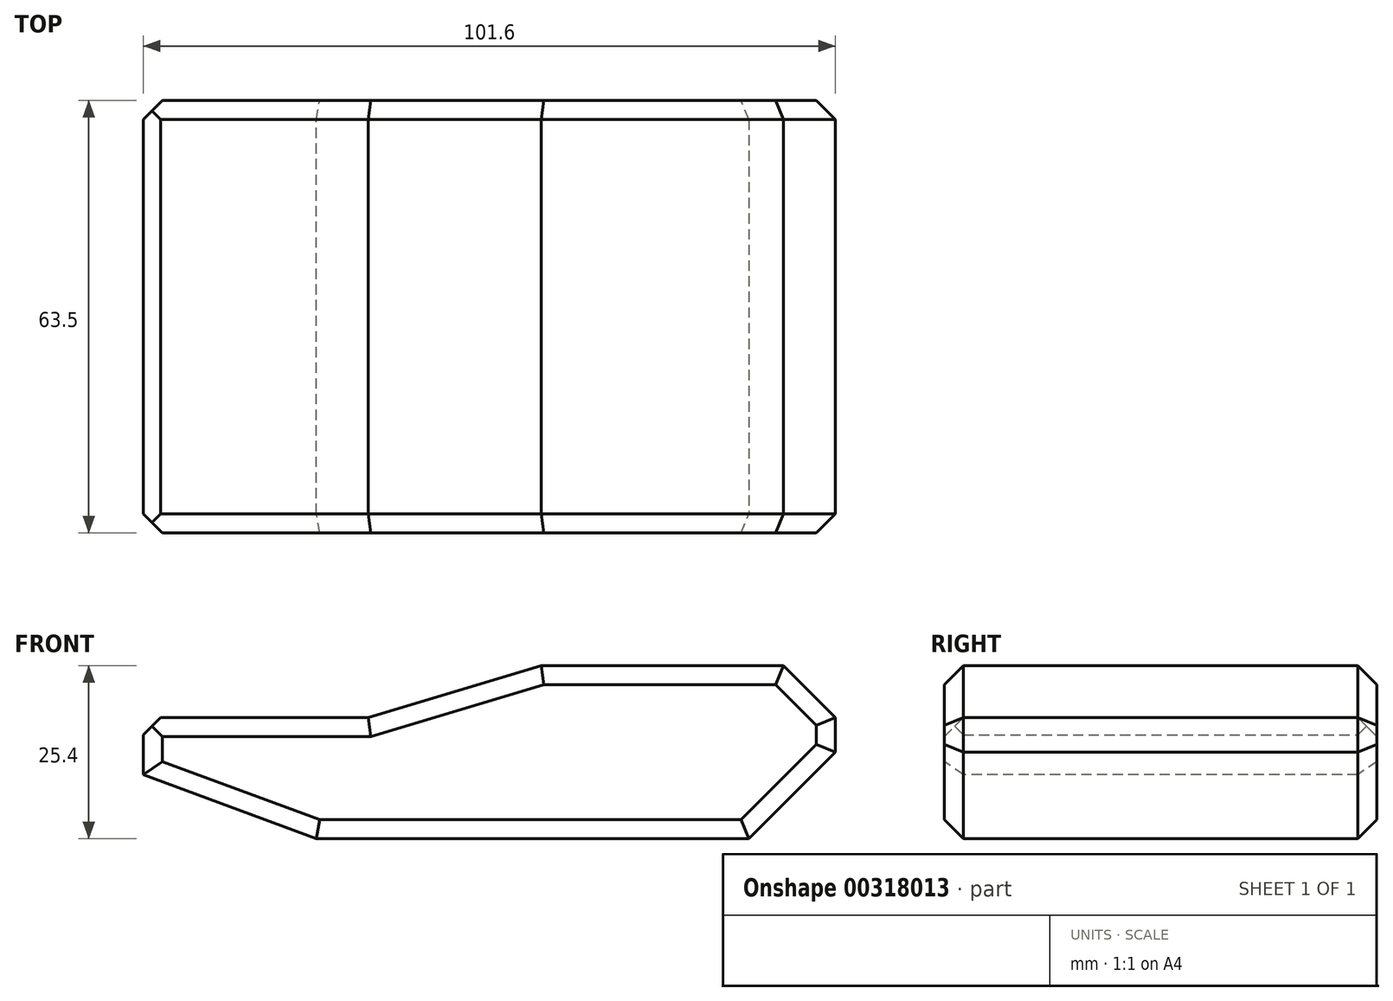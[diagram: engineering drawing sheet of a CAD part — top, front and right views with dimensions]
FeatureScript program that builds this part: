
annotation { "Feature Type Name" : "Feature", "Feature Type Description" : "" }
export const myFeature = defineFeature(function(context is Context, id is Id, definition is map)
    precondition{}
    {
        {
            var Q0;
            Q0=qCreatedBy(makeId("Front.planeOp"),FACE);
            var sketch = newSketch(context, id + "F0", { "sketchPlane" : qUnion([Q0])});
            skLineSegment(sketch, "E0.bottom", {"start": v(-65.25, 21.28) * mm, "end": v(36.35, 21.28) * mm});
            skLineSegment(sketch, "E0.top", {"start": v(-65.25, 3.5) * mm, "end": v(36.35, 3.5) * mm});
            skLineSegment(sketch, "E0.left", {"start": v(-65.25, 21.28) * mm, "end": v(-65.25, 3.5) * mm});
            skLineSegment(sketch, "E0.right", {"start": v(36.35, 21.28) * mm, "end": v(36.35, 3.5) * mm});
            skSolve(sketch);
        }
        {
            var Q0;
            Q0=makeQuery(id+"F0.imprint","IMPRINT",FACE,{"disambiguationData":[TD([[makeQuery(id+"F0.imprint","IMPRINT",EDGE,{"derivedFrom":sQuery(id+"F0.wireOp",EDGE,"E0.bottom")}),-1.0]])]});
            extrude(context, id + "F1", {"entities" : qUnion([Q0]), "depth" : 63.5 * mm});
        }
        {
            var Q0;
            Q0=makeQuery(id+"F1.opExtrude","SWEPT_EDGE",EDGE,{"disambiguationData":[OSD([sQuery(id+"F0.wireOp",EDGE,"E0.top"),sQuery(id+"F0.wireOp",EDGE,"E0.left")])]});
            chamfer(context, id + "F2", {"entities" : qUnion([Q0]), "chamferType" : ChamferType.TWO_OFFSETS, "width1" : 25.4 * mm, "oppositeDirection" : false, "width2" : 9.4 * mm, "tangentPropagation" : true});
        }
        {
            var Q0;
            Q0=makeQuery(id+"F1.opExtrude","SWEPT_EDGE",EDGE,{"disambiguationData":[OSD([sQuery(id+"F0.wireOp",EDGE,"E0.top"),sQuery(id+"F0.wireOp",EDGE,"E0.right")])]});
            chamfer(context, id + "F3", {"entities" : qUnion([Q0]), "width" : 12.7 * mm, "tangentPropagation" : true});
        }
        {
            var Q0;
            Q0=makeQuery(id+"F1.opExtrude","CAP_FACE",FACE,{"disambiguationData":[OSD([sQuery(id+"F0.wireOp",EDGE,"E0.bottom"),sQuery(id+"F0.wireOp",EDGE,"E0.top"),sQuery(id+"F0.wireOp",EDGE,"E0.left"),sQuery(id+"F0.wireOp",EDGE,"E0.right")])],"isStart":true});
            var sketch = newSketch(context, id + "F4", { "sketchPlane" : qUnion([Q0])});
            skLineSegment(sketch, "E1.bottom", {"start": v(-36.35, 21.28) * mm, "end": v(32.23, 21.28) * mm});
            skLineSegment(sketch, "E1.top", {"start": v(-36.35, 28.9) * mm, "end": v(32.23, 28.9) * mm});
            skLineSegment(sketch, "E1.left", {"start": v(-36.35, 21.28) * mm, "end": v(-36.35, 28.9) * mm});
            skLineSegment(sketch, "E1.right", {"start": v(32.23, 21.28) * mm, "end": v(32.23, 28.9) * mm});
            skSolve(sketch);
        }
        {
            var Q0;
            Q0=makeQuery(id+"F4.imprint","IMPRINT",FACE,{"disambiguationData":[TD([[makeQuery(id+"F4.imprint","IMPRINT",EDGE,{"derivedFrom":sQuery(id+"F4.wireOp",EDGE,"E1.bottom")}),-1.0]])]});
            extrude(context, id + "F5", {"entities" : qUnion([Q0]), "operationType" : NewBodyOperationType.ADD, "oppositeDirection" : true, "depth" : 63.5 * mm});
        }
        {
            var Q0;
            Q0=makeQuery(id+"F5.opExtrude","SWEPT_EDGE",EDGE,{"disambiguationData":[OSD([sQuery(id+"F4.wireOp",EDGE,"E1.top"),sQuery(id+"F4.wireOp",EDGE,"E1.left")])]});
            chamfer(context, id + "F6", {"entities" : qUnion([Q0]), "chamferType" : ChamferType.TWO_OFFSETS, "width1" : 7.62 * mm, "oppositeDirection" : false, "width2" : 7.62 * mm, "tangentPropagation" : true});
        }
        {
            var Q0;
            Q0=makeQuery(id+"F5.opExtrude","SWEPT_EDGE",EDGE,{"disambiguationData":[OSD([sQuery(id+"F4.wireOp",EDGE,"E1.top"),sQuery(id+"F4.wireOp",EDGE,"E1.right")])]});
            chamfer(context, id + "F7", {"entities" : qUnion([Q0]), "chamferType" : ChamferType.TWO_OFFSETS, "width1" : 7.62 * mm, "oppositeDirection" : false, "width2" : 25.4 * mm, "tangentPropagation" : true});
        }
        {
            var Q0;
            Q0=makeQuery(id+"F1.opExtrude","CAP_EDGE",EDGE,{"disambiguationData":[OSD([sQuery(id+"F0.wireOp",EDGE,"E0.left")])],"isStart":true});
            var Q1;
            Q1=makeQuery(id+"F1.opExtrude","CAP_EDGE",EDGE,{"disambiguationData":[OSD([sQuery(id+"F0.wireOp",EDGE,"E0.left")])],"isStart":false});
            var Q2;
            {var subQ0=sQuery(id+"F0.wireOp",EDGE,"E0.left");var subQ1=sQuery(id+"F0.wireOp",EDGE,"E0.top");Q2=makeQuery(id+"F2.opChamfer","BLEND_EDGE",EDGE,{"blendedFrom":[makeQuery(id+"F1.opExtrude","SWEPT_EDGE",EDGE,{"disambiguationData":[OSD([subQ1,subQ0])]}),makeQuery(id+"F1.opExtrude","CAP_FACE",FACE,{"disambiguationData":[OSD([sQuery(id+"F0.wireOp",EDGE,"E0.bottom"),subQ1,subQ0,sQuery(id+"F0.wireOp",EDGE,"E0.right")])],"isStart":false})],"blendedInto":[makeQuery(id+"F1.opExtrude","CAP_FACE",FACE,{"disambiguationData":[OSD([sQuery(id+"F0.wireOp",EDGE,"E0.bottom"),subQ1,subQ0,sQuery(id+"F0.wireOp",EDGE,"E0.right")])],"isStart":false})]});}
            var Q3;
            {var subQ0=sQuery(id+"F0.wireOp",EDGE,"E0.left");var subQ1=sQuery(id+"F0.wireOp",EDGE,"E0.top");Q3=makeQuery(id+"F2.opChamfer","BLEND_EDGE",EDGE,{"blendedFrom":[makeQuery(id+"F1.opExtrude","SWEPT_EDGE",EDGE,{"disambiguationData":[OSD([subQ1,subQ0])]}),makeQuery(id+"F1.opExtrude","CAP_FACE",FACE,{"disambiguationData":[OSD([sQuery(id+"F0.wireOp",EDGE,"E0.bottom"),subQ1,subQ0,sQuery(id+"F0.wireOp",EDGE,"E0.right")])],"isStart":true})],"blendedInto":[makeQuery(id+"F1.opExtrude","CAP_FACE",FACE,{"disambiguationData":[OSD([sQuery(id+"F0.wireOp",EDGE,"E0.bottom"),subQ1,subQ0,sQuery(id+"F0.wireOp",EDGE,"E0.right")])],"isStart":true})]});}
            var Q4;
            Q4=makeQuery(id+"F1.opExtrude","CAP_EDGE",EDGE,{"disambiguationData":[OSD([sQuery(id+"F0.wireOp",EDGE,"E0.top")])],"isStart":true});
            var Q5;
            Q5=makeQuery(id+"F1.opExtrude","CAP_EDGE",EDGE,{"disambiguationData":[OSD([sQuery(id+"F0.wireOp",EDGE,"E0.top")])],"isStart":false});
            var Q6;
            {var subQ0=sQuery(id+"F4.wireOp",EDGE,"E1.left");var subQ1=sQuery(id+"F4.wireOp",EDGE,"E1.top");Q6=makeQuery(id+"F6.opChamfer","BLEND_EDGE",EDGE,{"blendedFrom":[makeQuery(id+"F5.opExtrude","SWEPT_EDGE",EDGE,{"disambiguationData":[OSD([subQ1,subQ0])]}),makeQuery(id+"F5.boolean.opBoolean","MERGE",FACE,{"derivedFrom":[makeQuery(id+"F1.opExtrude","CAP_FACE",FACE,{"disambiguationData":[OSD([sQuery(id+"F0.wireOp",EDGE,"E0.bottom"),sQuery(id+"F0.wireOp",EDGE,"E0.top"),sQuery(id+"F0.wireOp",EDGE,"E0.left"),sQuery(id+"F0.wireOp",EDGE,"E0.right")])],"isStart":false}),makeQuery(id+"F5.opExtrude","CAP_FACE",FACE,{"disambiguationData":[OSD([sQuery(id+"F4.wireOp",EDGE,"E1.bottom"),subQ1,subQ0,sQuery(id+"F4.wireOp",EDGE,"E1.right")])],"isStart":false})]})],"blendedInto":[makeQuery(id+"F5.boolean.opBoolean","MERGE",FACE,{"derivedFrom":[makeQuery(id+"F1.opExtrude","CAP_FACE",FACE,{"disambiguationData":[OSD([sQuery(id+"F0.wireOp",EDGE,"E0.bottom"),sQuery(id+"F0.wireOp",EDGE,"E0.top"),sQuery(id+"F0.wireOp",EDGE,"E0.left"),sQuery(id+"F0.wireOp",EDGE,"E0.right")])],"isStart":false}),makeQuery(id+"F5.opExtrude","CAP_FACE",FACE,{"disambiguationData":[OSD([sQuery(id+"F4.wireOp",EDGE,"E1.bottom"),subQ1,subQ0,sQuery(id+"F4.wireOp",EDGE,"E1.right")])],"isStart":false})]})]});}
            var Q7;
            Q7=makeQuery(id+"F5.boolean.opBoolean","MERGE",EDGE,{"derivedFrom":[makeQuery(id+"F1.opExtrude","CAP_EDGE",EDGE,{"disambiguationData":[OSD([sQuery(id+"F0.wireOp",EDGE,"E0.right")])],"isStart":false}),makeQuery(id+"F5.opExtrude","CAP_EDGE",EDGE,{"disambiguationData":[OSD([sQuery(id+"F4.wireOp",EDGE,"E1.left")])],"isStart":false})]});
            var Q8;
            {var subQ0=sQuery(id+"F0.wireOp",EDGE,"E0.right");var subQ1=sQuery(id+"F0.wireOp",EDGE,"E0.top");Q8=makeQuery(id+"F3.opChamfer","BLEND_EDGE",EDGE,{"blendedFrom":[makeQuery(id+"F1.opExtrude","SWEPT_EDGE",EDGE,{"disambiguationData":[OSD([subQ1,subQ0])]}),makeQuery(id+"F1.opExtrude","CAP_FACE",FACE,{"disambiguationData":[OSD([sQuery(id+"F0.wireOp",EDGE,"E0.bottom"),subQ1,sQuery(id+"F0.wireOp",EDGE,"E0.left"),subQ0])],"isStart":false})],"blendedInto":[makeQuery(id+"F1.opExtrude","CAP_FACE",FACE,{"disambiguationData":[OSD([sQuery(id+"F0.wireOp",EDGE,"E0.bottom"),subQ1,sQuery(id+"F0.wireOp",EDGE,"E0.left"),subQ0])],"isStart":false})]});}
            var Q9;
            {var subQ0=sQuery(id+"F0.wireOp",EDGE,"E0.right");var subQ1=sQuery(id+"F0.wireOp",EDGE,"E0.top");Q9=makeQuery(id+"F3.opChamfer","BLEND_EDGE",EDGE,{"blendedFrom":[makeQuery(id+"F1.opExtrude","SWEPT_EDGE",EDGE,{"disambiguationData":[OSD([subQ1,subQ0])]}),makeQuery(id+"F1.opExtrude","CAP_FACE",FACE,{"disambiguationData":[OSD([sQuery(id+"F0.wireOp",EDGE,"E0.bottom"),subQ1,sQuery(id+"F0.wireOp",EDGE,"E0.left"),subQ0])],"isStart":true})],"blendedInto":[makeQuery(id+"F1.opExtrude","CAP_FACE",FACE,{"disambiguationData":[OSD([sQuery(id+"F0.wireOp",EDGE,"E0.bottom"),subQ1,sQuery(id+"F0.wireOp",EDGE,"E0.left"),subQ0])],"isStart":true})]});}
            var Q10;
            Q10=makeQuery(id+"F5.boolean.opBoolean","MERGE",EDGE,{"derivedFrom":[makeQuery(id+"F1.opExtrude","CAP_EDGE",EDGE,{"disambiguationData":[OSD([sQuery(id+"F0.wireOp",EDGE,"E0.right")])],"isStart":true}),makeQuery(id+"F5.opExtrude","CAP_EDGE",EDGE,{"disambiguationData":[OSD([sQuery(id+"F4.wireOp",EDGE,"E1.left")])],"isStart":true})]});
            var Q11;
            {var subQ0=sQuery(id+"F4.wireOp",EDGE,"E1.left");var subQ1=sQuery(id+"F4.wireOp",EDGE,"E1.top");Q11=makeQuery(id+"F6.opChamfer","BLEND_EDGE",EDGE,{"blendedFrom":[makeQuery(id+"F5.opExtrude","SWEPT_EDGE",EDGE,{"disambiguationData":[OSD([subQ1,subQ0])]}),makeQuery(id+"F5.boolean.opBoolean","MERGE",FACE,{"derivedFrom":[makeQuery(id+"F1.opExtrude","CAP_FACE",FACE,{"disambiguationData":[OSD([sQuery(id+"F0.wireOp",EDGE,"E0.bottom"),sQuery(id+"F0.wireOp",EDGE,"E0.top"),sQuery(id+"F0.wireOp",EDGE,"E0.left"),sQuery(id+"F0.wireOp",EDGE,"E0.right")])],"isStart":true}),makeQuery(id+"F5.opExtrude","CAP_FACE",FACE,{"disambiguationData":[OSD([sQuery(id+"F4.wireOp",EDGE,"E1.bottom"),subQ1,subQ0,sQuery(id+"F4.wireOp",EDGE,"E1.right")])],"isStart":true})]})],"blendedInto":[makeQuery(id+"F5.boolean.opBoolean","MERGE",FACE,{"derivedFrom":[makeQuery(id+"F1.opExtrude","CAP_FACE",FACE,{"disambiguationData":[OSD([sQuery(id+"F0.wireOp",EDGE,"E0.bottom"),sQuery(id+"F0.wireOp",EDGE,"E0.top"),sQuery(id+"F0.wireOp",EDGE,"E0.left"),sQuery(id+"F0.wireOp",EDGE,"E0.right")])],"isStart":true}),makeQuery(id+"F5.opExtrude","CAP_FACE",FACE,{"disambiguationData":[OSD([sQuery(id+"F4.wireOp",EDGE,"E1.bottom"),subQ1,subQ0,sQuery(id+"F4.wireOp",EDGE,"E1.right")])],"isStart":true})]})]});}
            var Q12;
            Q12=makeQuery(id+"F5.opExtrude","CAP_EDGE",EDGE,{"disambiguationData":[OSD([sQuery(id+"F4.wireOp",EDGE,"E1.top")])],"isStart":true});
            var Q13;
            {var subQ0=sQuery(id+"F4.wireOp",EDGE,"E1.right");var subQ1=sQuery(id+"F4.wireOp",EDGE,"E1.top");Q13=makeQuery(id+"F7.opChamfer","BLEND_EDGE",EDGE,{"blendedFrom":[makeQuery(id+"F5.opExtrude","SWEPT_EDGE",EDGE,{"disambiguationData":[OSD([subQ1,subQ0])]}),makeQuery(id+"F5.boolean.opBoolean","MERGE",FACE,{"derivedFrom":[makeQuery(id+"F1.opExtrude","CAP_FACE",FACE,{"disambiguationData":[OSD([sQuery(id+"F0.wireOp",EDGE,"E0.bottom"),sQuery(id+"F0.wireOp",EDGE,"E0.top"),sQuery(id+"F0.wireOp",EDGE,"E0.left"),sQuery(id+"F0.wireOp",EDGE,"E0.right")])],"isStart":true}),makeQuery(id+"F5.opExtrude","CAP_FACE",FACE,{"disambiguationData":[OSD([sQuery(id+"F4.wireOp",EDGE,"E1.bottom"),subQ1,sQuery(id+"F4.wireOp",EDGE,"E1.left"),subQ0])],"isStart":true})]})],"blendedInto":[makeQuery(id+"F5.boolean.opBoolean","MERGE",FACE,{"derivedFrom":[makeQuery(id+"F1.opExtrude","CAP_FACE",FACE,{"disambiguationData":[OSD([sQuery(id+"F0.wireOp",EDGE,"E0.bottom"),sQuery(id+"F0.wireOp",EDGE,"E0.top"),sQuery(id+"F0.wireOp",EDGE,"E0.left"),sQuery(id+"F0.wireOp",EDGE,"E0.right")])],"isStart":true}),makeQuery(id+"F5.opExtrude","CAP_FACE",FACE,{"disambiguationData":[OSD([sQuery(id+"F4.wireOp",EDGE,"E1.bottom"),subQ1,sQuery(id+"F4.wireOp",EDGE,"E1.left"),subQ0])],"isStart":true})]})]});}
            var Q14;
            Q14=makeQuery(id+"F1.opExtrude","CAP_EDGE",EDGE,{"disambiguationData":[OSD([sQuery(id+"F0.wireOp",EDGE,"E0.bottom")])],"isStart":true});
            var Q15;
            {var subQ0=sQuery(id+"F4.wireOp",EDGE,"E1.right");var subQ1=sQuery(id+"F4.wireOp",EDGE,"E1.top");Q15=makeQuery(id+"F7.opChamfer","BLEND_EDGE",EDGE,{"blendedFrom":[makeQuery(id+"F5.opExtrude","SWEPT_EDGE",EDGE,{"disambiguationData":[OSD([subQ1,subQ0])]}),makeQuery(id+"F5.boolean.opBoolean","MERGE",FACE,{"derivedFrom":[makeQuery(id+"F1.opExtrude","CAP_FACE",FACE,{"disambiguationData":[OSD([sQuery(id+"F0.wireOp",EDGE,"E0.bottom"),sQuery(id+"F0.wireOp",EDGE,"E0.top"),sQuery(id+"F0.wireOp",EDGE,"E0.left"),sQuery(id+"F0.wireOp",EDGE,"E0.right")])],"isStart":false}),makeQuery(id+"F5.opExtrude","CAP_FACE",FACE,{"disambiguationData":[OSD([sQuery(id+"F4.wireOp",EDGE,"E1.bottom"),subQ1,sQuery(id+"F4.wireOp",EDGE,"E1.left"),subQ0])],"isStart":false})]})],"blendedInto":[makeQuery(id+"F5.boolean.opBoolean","MERGE",FACE,{"derivedFrom":[makeQuery(id+"F1.opExtrude","CAP_FACE",FACE,{"disambiguationData":[OSD([sQuery(id+"F0.wireOp",EDGE,"E0.bottom"),sQuery(id+"F0.wireOp",EDGE,"E0.top"),sQuery(id+"F0.wireOp",EDGE,"E0.left"),sQuery(id+"F0.wireOp",EDGE,"E0.right")])],"isStart":false}),makeQuery(id+"F5.opExtrude","CAP_FACE",FACE,{"disambiguationData":[OSD([sQuery(id+"F4.wireOp",EDGE,"E1.bottom"),subQ1,sQuery(id+"F4.wireOp",EDGE,"E1.left"),subQ0])],"isStart":false})]})]});}
            var Q16;
            Q16=makeQuery(id+"F5.opExtrude","CAP_EDGE",EDGE,{"disambiguationData":[OSD([sQuery(id+"F4.wireOp",EDGE,"E1.top")])],"isStart":false});
            var Q17;
            Q17=makeQuery(id+"F1.opExtrude","CAP_EDGE",EDGE,{"disambiguationData":[OSD([sQuery(id+"F0.wireOp",EDGE,"E0.bottom")])],"isStart":false});
            chamfer(context, id + "F8", {"entities" : qUnion([Q0, Q1, Q2, Q3, Q4, Q5, Q6, Q7, Q8, Q9, Q10, Q11, Q12, Q13, Q14, Q15, Q16, Q17]), "width" : 2.8 * mm, "tangentPropagation" : true});
        }
        {
            var Q0;
            Q0=makeQuery(id+"F1.opExtrude","SWEPT_EDGE",EDGE,{"disambiguationData":[OSD([sQuery(id+"F0.wireOp",EDGE,"E0.bottom"),sQuery(id+"F0.wireOp",EDGE,"E0.left")])]});
            chamfer(context, id + "F9", {"entities" : qUnion([Q0]), "width" : 2.54 * mm, "tangentPropagation" : true});
        }
    });
